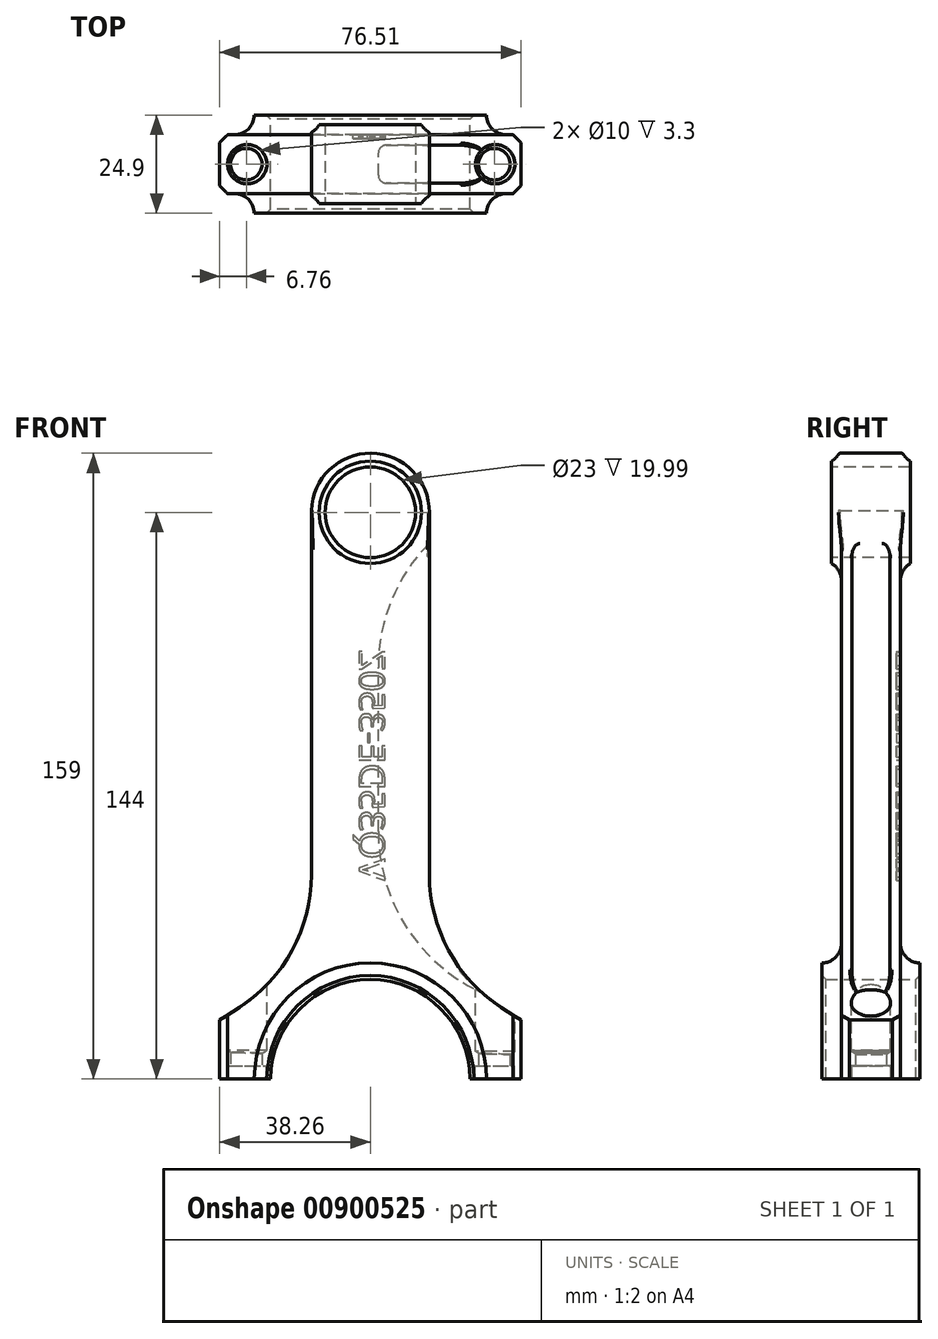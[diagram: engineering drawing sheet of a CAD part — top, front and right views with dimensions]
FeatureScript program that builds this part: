
annotation { "Feature Type Name" : "Feature", "Feature Type Description" : "" }
export const myFeature = defineFeature(function(context is Context, id is Id, definition is map)
    precondition{}
    {
        {
            var Q0;
            Q0=qCreatedBy(makeId("Front.planeOp"),FACE);
            var sketch = newSketch(context, id + "F0", { "sketchPlane" : qUnion([Q0])});
            skArc(sketch, "E0", {"start": v(15, 144) * mm, "mid": v(0.23, 159) * mm, "end": v(-15, 144.46) * mm});
            skLineSegment(sketch, "E1", {"start": v(25.3, 0) * mm, "end": v(38.25, 0) * mm});
            skArc(sketch, "E2", {"start": v(-15, 51.82) * mm, "mid": v(-19.85, 32.73) * mm, "end": v(-33.22, 18.27) * mm});
            skArc(sketch, "E3.MirrorCS", {"start": v(15, 51.82) * mm, "mid": v(19.85, 32.73) * mm, "end": v(33.22, 18.27) * mm});
            skLineSegment(sketch, "E4", {"start": v(-38.25, 0) * mm, "end": v(-25.3, 0) * mm});
            skArc(sketch, "E5", {"start": v(-25.3, 0) * mm, "mid": v(0, 25.3) * mm, "end": v(25.3, 0) * mm});
            skLineSegment(sketch, "E6", {"start": v(15, 144) * mm, "end": v(15, 51.82) * mm});
            skLineSegment(sketch, "E7", {"start": v(-15, 144.46) * mm, "end": v(-15, 51.82) * mm});
            skLineSegment(sketch, "E8", {"start": v(33.22, 18.27) * mm, "end": v(38.24, 15) * mm});
            skLineSegment(sketch, "E9", {"start": v(-33.22, 18.27) * mm, "end": v(-38.26, 15) * mm});
            skLineSegment(sketch, "E10", {"start": v(-38.25, 0) * mm, "end": v(-38.26, 15) * mm});
            skLineSegment(sketch, "E11", {"start": v(38.25, 0) * mm, "end": v(38.24, 15) * mm});
            skSolve(sketch);
        }
        {
            var Q0;
            Q0=makeQuery(id+"F0.imprint","IMPRINT",FACE,{"disambiguationData":[TD([[makeQuery(id+"F0.imprint","IMPRINT",EDGE,{"derivedFrom":sQuery(id+"F0.wireOp",EDGE,"E0")}),1.0]])]});
            extrude(context, id + "F1", {"entities" : qUnion([Q0]), "endBound" : BoundingType.SYMMETRIC, "depth" : 15 * mm, "offsetDistance" : 25 * mm});
        }
        {
            var Q0;
            Q0=qCreatedBy(makeId("Front.planeOp"),FACE);
            var sketch = newSketch(context, id + "F2", { "sketchPlane" : qUnion([Q0])});
            skCircle(sketch, "E12", {"center": v(0, 144) * mm, "radius": 13 * mm});
            skSolve(sketch);
        }
        {
            var Q0;
            Q0 = qSketchRegion(id + "F2", true);
            extrude(context, id + "F3", {"entities" : qUnion([Q0]), "operationType" : NewBodyOperationType.ADD, "endBound" : BoundingType.SYMMETRIC, "depth" : 19.99 * mm, "offsetDistance" : 25 * mm});
        }
        {
            var Q0;
            Q0=qCreatedBy(makeId("Front.planeOp"),FACE);
            var sketch = newSketch(context, id + "F4", { "sketchPlane" : qUnion([Q0])});
            skArc(sketch, "E13", {"start": v(29.5, 0) * mm, "mid": v(0, 29.5) * mm, "end": v(-29.5, 0) * mm});
            skArc(sketch, "E14", {"start": v(-25.3, 0) * mm, "mid": v(0, 25.3) * mm, "end": v(25.3, 0) * mm});
            skLineSegment(sketch, "E15", {"start": v(-29.5, 0) * mm, "end": v(-25.3, 0) * mm});
            skLineSegment(sketch, "E16", {"start": v(25.3, 0) * mm, "end": v(29.5, 0) * mm});
            skSolve(sketch);
        }
        {
            var Q0;
            Q0 = qSketchRegion(id + "F4", true);
            extrude(context, id + "F5", {"entities" : qUnion([Q0]), "operationType" : NewBodyOperationType.ADD, "endBound" : BoundingType.SYMMETRIC, "depth" : 24.9 * mm, "offsetDistance" : 25 * mm});
        }
        {
            var Q0;
            Q0=makeQuery(id+"F5.boolean.opBoolean","INTERSECT",EDGE,{"derivedFrom":[makeQuery(id+"F1.opExtrude","CAP_FACE",FACE,{"disambiguationData":[OSD([sQuery(id+"F0.wireOp",EDGE,"E0"),sQuery(id+"F0.wireOp",EDGE,"E1"),sQuery(id+"F0.wireOp",EDGE,"E2"),sQuery(id+"F0.wireOp",EDGE,"E3.MirrorCS"),sQuery(id+"F0.wireOp",EDGE,"E4"),sQuery(id+"F0.wireOp",EDGE,"E5"),sQuery(id+"F0.wireOp",EDGE,"E6"),sQuery(id+"F0.wireOp",EDGE,"E7"),sQuery(id+"F0.wireOp",EDGE,"E8"),sQuery(id+"F0.wireOp",EDGE,"E9"),sQuery(id+"F0.wireOp",EDGE,"E10"),sQuery(id+"F0.wireOp",EDGE,"E11")])],"isStart":false}),makeQuery(id+"F5.opExtrude","SWEPT_FACE",FACE,{"disambiguationData":[OSD([sQuery(id+"F4.wireOp",EDGE,"E13")])]})]});
            var Q1;
            Q1=makeQuery(id+"F3.boolean.opBoolean","INTERSECT",EDGE,{"derivedFrom":[makeQuery(id+"F1.opExtrude","CAP_FACE",FACE,{"disambiguationData":[OSD([sQuery(id+"F0.wireOp",EDGE,"E0"),sQuery(id+"F0.wireOp",EDGE,"E1"),sQuery(id+"F0.wireOp",EDGE,"E2"),sQuery(id+"F0.wireOp",EDGE,"E3.MirrorCS"),sQuery(id+"F0.wireOp",EDGE,"E4"),sQuery(id+"F0.wireOp",EDGE,"E5"),sQuery(id+"F0.wireOp",EDGE,"E6"),sQuery(id+"F0.wireOp",EDGE,"E7"),sQuery(id+"F0.wireOp",EDGE,"E8"),sQuery(id+"F0.wireOp",EDGE,"E9"),sQuery(id+"F0.wireOp",EDGE,"E10"),sQuery(id+"F0.wireOp",EDGE,"E11")])],"isStart":false}),makeQuery(id+"F3.opExtrude","SWEPT_FACE",FACE,{"disambiguationData":[OSD([sQuery(id+"F2.wireOp",EDGE,"E12")])]})]});
            var Q2;
            Q2=makeQuery(id+"F3.boolean.opBoolean","INTERSECT",EDGE,{"derivedFrom":[makeQuery(id+"F1.opExtrude","CAP_FACE",FACE,{"disambiguationData":[OSD([sQuery(id+"F0.wireOp",EDGE,"E0"),sQuery(id+"F0.wireOp",EDGE,"E1"),sQuery(id+"F0.wireOp",EDGE,"E2"),sQuery(id+"F0.wireOp",EDGE,"E3.MirrorCS"),sQuery(id+"F0.wireOp",EDGE,"E4"),sQuery(id+"F0.wireOp",EDGE,"E5"),sQuery(id+"F0.wireOp",EDGE,"E6"),sQuery(id+"F0.wireOp",EDGE,"E7"),sQuery(id+"F0.wireOp",EDGE,"E8"),sQuery(id+"F0.wireOp",EDGE,"E9"),sQuery(id+"F0.wireOp",EDGE,"E10"),sQuery(id+"F0.wireOp",EDGE,"E11")])],"isStart":true}),makeQuery(id+"F3.opExtrude","SWEPT_FACE",FACE,{"disambiguationData":[OSD([sQuery(id+"F2.wireOp",EDGE,"E12")])]})]});
            var Q3;
            Q3=makeQuery(id+"F5.boolean.opBoolean","INTERSECT",EDGE,{"derivedFrom":[makeQuery(id+"F1.opExtrude","CAP_FACE",FACE,{"disambiguationData":[OSD([sQuery(id+"F0.wireOp",EDGE,"E0"),sQuery(id+"F0.wireOp",EDGE,"E1"),sQuery(id+"F0.wireOp",EDGE,"E2"),sQuery(id+"F0.wireOp",EDGE,"E3.MirrorCS"),sQuery(id+"F0.wireOp",EDGE,"E4"),sQuery(id+"F0.wireOp",EDGE,"E5"),sQuery(id+"F0.wireOp",EDGE,"E6"),sQuery(id+"F0.wireOp",EDGE,"E7"),sQuery(id+"F0.wireOp",EDGE,"E8"),sQuery(id+"F0.wireOp",EDGE,"E9"),sQuery(id+"F0.wireOp",EDGE,"E10"),sQuery(id+"F0.wireOp",EDGE,"E11")])],"isStart":true}),makeQuery(id+"F5.opExtrude","SWEPT_FACE",FACE,{"disambiguationData":[OSD([sQuery(id+"F4.wireOp",EDGE,"E13")])]})]});
            fillet(context, id + "F6", {"entities" : qUnion([Q0, Q1, Q2, Q3]), "radius" : 5 * mm, "tangentPropagation" : true, "allowEdgeOverflow" : false});
        }
        {
            var Q0;
            Q0=makeQuery(id+"F5.boolean.opBoolean","MERGE",FACE,{"derivedFrom":[makeQuery(id+"F1.opExtrude","SWEPT_FACE",FACE,{"disambiguationData":[OSD([sQuery(id+"F0.wireOp",EDGE,"E4")])]}),makeQuery(id+"F5.opExtrude","SWEPT_FACE",FACE,{"disambiguationData":[OSD([sQuery(id+"F4.wireOp",EDGE,"E15")])]})]});
            var sketch = newSketch(context, id + "F7", { "sketchPlane" : qUnion([Q0])});
            skPoint(sketch, "E17", {"position": v(-31.5, 0) * mm});
            skPoint(sketch, "E18", {"position": v(31.5, 0) * mm});
            skSolve(sketch);
        }
        {
            var Q0;
            Q0=sQuery(id+"F7.wireOp",VERTEX,"E17");
            var Q1;
            Q1=sQuery(id+"F7.wireOp",VERTEX,"E18");
            var Q2;
            Q2=makeQuery(id+"F1.opExtrude","SWEPT_BODY",BODY,{"disambiguationData":[OSD([sQuery(id+"F0.wireOp",EDGE,"E0"),sQuery(id+"F0.wireOp",EDGE,"E1"),sQuery(id+"F0.wireOp",EDGE,"E2"),sQuery(id+"F0.wireOp",EDGE,"E3.MirrorCS"),sQuery(id+"F0.wireOp",EDGE,"E4"),sQuery(id+"F0.wireOp",EDGE,"E5"),sQuery(id+"F0.wireOp",EDGE,"E6"),sQuery(id+"F0.wireOp",EDGE,"E7"),sQuery(id+"F0.wireOp",EDGE,"E8"),sQuery(id+"F0.wireOp",EDGE,"E9"),sQuery(id+"F0.wireOp",EDGE,"E10"),sQuery(id+"F0.wireOp",EDGE,"E11")])]});
            hole(context, id + "F8", {"style" : HoleStyle.C_BORE, "endStyle" : HoleEndStyle.THROUGH, "holeDiameter" : 8 * mm, "cBoreDiameter" : 10 * mm, "cBoreDepth" : 3.3 * mm, "majorDiameter" : 5 * mm, "isTappedThrough" : true, "tappedDepth" : 12 * mm, "tapClearance" : 3, "locations" : qUnion([Q0, Q1]), "scope" : qUnion([Q2])});
        }
        {
            var Q0;
            Q0=makeQuery(id+"F5.boolean.opBoolean","MERGE",FACE,{"derivedFrom":[makeQuery(id+"F1.opExtrude","SWEPT_FACE",FACE,{"disambiguationData":[OSD([sQuery(id+"F0.wireOp",EDGE,"E4")])]}),makeQuery(id+"F5.opExtrude","SWEPT_FACE",FACE,{"disambiguationData":[OSD([sQuery(id+"F4.wireOp",EDGE,"E15")])]})]});
            cPlane(context, id + "F9", {"entities" : qUnion([Q0]), "cplaneType" : CPlaneType.OFFSET, "offset" : 25 * mm, "oppositeDirection" : true, "width" : 150 * mm, "height" : 150 * mm});
        }
        {
            var Q0;
            Q0=qCreatedBy(id+"F9.planeOp",FACE);
            var sketch = newSketch(context, id + "F10", { "sketchPlane" : qUnion([Q0])});
            skPoint(sketch, "E19", {"position": v(-31.27, 0) * mm});
            skPoint(sketch, "E20", {"position": v(31.73, 0) * mm});
            skSolve(sketch);
        }
        {
            var Q0;
            Q0=sQuery(id+"F10.wireOp",VERTEX,"E19");
            var Q1;
            Q1=sQuery(id+"F10.wireOp",VERTEX,"E20");
            var Q2;
            Q2=makeQuery(id+"F1.opExtrude","SWEPT_BODY",BODY,{"disambiguationData":[OSD([sQuery(id+"F0.wireOp",EDGE,"E0"),sQuery(id+"F0.wireOp",EDGE,"E1"),sQuery(id+"F0.wireOp",EDGE,"E2"),sQuery(id+"F0.wireOp",EDGE,"E3.MirrorCS"),sQuery(id+"F0.wireOp",EDGE,"E4"),sQuery(id+"F0.wireOp",EDGE,"E5"),sQuery(id+"F0.wireOp",EDGE,"E6"),sQuery(id+"F0.wireOp",EDGE,"E7"),sQuery(id+"F0.wireOp",EDGE,"E8"),sQuery(id+"F0.wireOp",EDGE,"E9"),sQuery(id+"F0.wireOp",EDGE,"E10"),sQuery(id+"F0.wireOp",EDGE,"E11")])]});
            hole(context, id + "F11", {"style" : HoleStyle.SIMPLE, "endStyle" : HoleEndStyle.BLIND, "oppositeDirection" : true, "holeDiameter" : 10 * mm, "majorDiameter" : 5 * mm, "holeDepth" : 9 * mm, "isTappedThrough" : true, "tappedDepth" : 12 * mm, "tapClearance" : 3, "locations" : qUnion([Q0, Q1]), "scope" : qUnion([Q2])});
        }
        {
            var Q0;
            Q0=makeQuery(id+"F3.opExtrude","CAP_FACE",FACE,{"disambiguationData":[OSD([sQuery(id+"F2.wireOp",EDGE,"E12")])],"isStart":false});
            var sketch = newSketch(context, id + "F12", { "sketchPlane" : qUnion([Q0])});
            skPoint(sketch, "E21", {"position": v(0, 144) * mm});
            skSolve(sketch);
        }
        {
            var Q0;
            Q0=sQuery(id+"F12.wireOp",VERTEX,"E21");
            var Q1;
            Q1=makeQuery(id+"F1.opExtrude","SWEPT_BODY",BODY,{"disambiguationData":[OSD([sQuery(id+"F0.wireOp",EDGE,"E0"),sQuery(id+"F0.wireOp",EDGE,"E1"),sQuery(id+"F0.wireOp",EDGE,"E2"),sQuery(id+"F0.wireOp",EDGE,"E3.MirrorCS"),sQuery(id+"F0.wireOp",EDGE,"E4"),sQuery(id+"F0.wireOp",EDGE,"E5"),sQuery(id+"F0.wireOp",EDGE,"E6"),sQuery(id+"F0.wireOp",EDGE,"E7"),sQuery(id+"F0.wireOp",EDGE,"E8"),sQuery(id+"F0.wireOp",EDGE,"E9"),sQuery(id+"F0.wireOp",EDGE,"E10"),sQuery(id+"F0.wireOp",EDGE,"E11")])]});
            hole(context, id + "F13", {"style" : HoleStyle.SIMPLE, "endStyle" : HoleEndStyle.THROUGH, "holeDiameter" : 23 * mm, "majorDiameter" : 5 * mm, "isTappedThrough" : true, "tappedDepth" : 12 * mm, "tapClearance" : 3, "locations" : qUnion([Q0]), "scope" : qUnion([Q1])});
        }
        {
            var Q0;
            Q0=qCreatedBy(makeId("Front.planeOp"),FACE);
            var sketch = newSketch(context, id + "F14", { "sketchPlane" : qUnion([Q0])});
            skArc(sketch, "E22", {"start": v(2.03, 62.88) * mm, "mid": v(9.36, 38.26) * mm, "end": v(28.96, 21.67) * mm});
            skCircle(sketch, "E23", {"center": v(0, 0) * mm, "radius": 25.3 * mm, "construction": true});
            skLineSegment(sketch, "E24", {"start": v(29.55, 7.8) * mm, "end": v(-8.31, 40.83) * mm, "construction": true});
            skLineSegment(sketch, "E25", {"start": v(35.49, 13.23) * mm, "end": v(-8.31, 51.45) * mm, "construction": true});
            skArc(sketch, "E26", {"start": v(15, 136.23) * mm, "mid": v(5.4, 121.7) * mm, "end": v(2.03, 104.62) * mm});
            skLineSegment(sketch, "E27", {"start": v(2.03, 62.88) * mm, "end": v(2.03, 104.62) * mm});
            skArc(sketch, "E28", {"start": v(15, 52.03) * mm, "mid": v(18.66, 35.32) * mm, "end": v(28.96, 21.67) * mm});
            skLineSegment(sketch, "E29.0", {"start": v(15, 136.23) * mm, "end": v(15, 51.82) * mm});
            skPoint(sketch, "E30.orphan", {"position": v(15, 144) * mm});
            skLineSegment(sketch, "E31", {"start": v(0, 0) * mm, "end": v(0, 56.7) * mm, "construction": true});
            skArc(sketch, "E32.MirrorCS", {"start": v(-2.03, 62.88) * mm, "mid": v(-9.36, 38.26) * mm, "end": v(-28.96, 21.67) * mm});
            skLineSegment(sketch, "E33.MirrorCS", {"start": v(-2.03, 62.88) * mm, "end": v(-2.03, 104.62) * mm});
            skArc(sketch, "E34.MirrorCS", {"start": v(-15, 136.23) * mm, "mid": v(-5.4, 121.7) * mm, "end": v(-2.03, 104.62) * mm});
            skLineSegment(sketch, "E35.MirrorCS", {"start": v(-15, 136.23) * mm, "end": v(-15, 51.82) * mm});
            skArc(sketch, "E36.MirrorCS", {"start": v(-15, 52.03) * mm, "mid": v(-18.66, 35.32) * mm, "end": v(-28.96, 21.67) * mm});
            skSolve(sketch);
        }
        {
            var Q0;
            Q0=makeQuery(id+"F14.imprint","IMPRINT",FACE,{"disambiguationData":[TD([[makeQuery(id+"F14.imprint","IMPRINT",EDGE,{"derivedFrom":sQuery(id+"F14.wireOp",EDGE,"E22")}),1.0]])]});
            var Q1;
            Q1=makeQuery(id+"F14.imprint","IMPRINT",FACE,{"disambiguationData":[TD([[makeQuery(id+"F14.imprint","IMPRINT",EDGE,{"derivedFrom":sQuery(id+"F14.wireOp",EDGE,"E32.MirrorCS")}),-1.0]])]});
            extrude(context, id + "F15", {"entities" : qUnion([Q0, Q1]), "operationType" : NewBodyOperationType.REMOVE, "endBound" : BoundingType.SYMMETRIC, "depth" : 9.65 * mm, "offsetDistance" : 25 * mm});
        }
        {
            var Q0;
            Q0=makeQuery(id+"F15.boolean.opBoolean","COPY",EDGE,{"derivedFrom":makeQuery(id+"F15.opExtrude","CAP_EDGE",EDGE,{"disambiguationData":[OSD([sQuery(id+"F14.wireOp",EDGE,"E33.MirrorCS")])],"isStart":false})});
            var Q1;
            Q1=makeQuery(id+"F15.boolean.opBoolean","COPY",EDGE,{"derivedFrom":makeQuery(id+"F15.opExtrude","CAP_EDGE",EDGE,{"disambiguationData":[OSD([sQuery(id+"F14.wireOp",EDGE,"E33.MirrorCS")])],"isStart":true})});
            var Q2;
            Q2=makeQuery(id+"F15.boolean.opBoolean","COPY",EDGE,{"derivedFrom":makeQuery(id+"F15.opExtrude","CAP_EDGE",EDGE,{"disambiguationData":[OSD([sQuery(id+"F14.wireOp",EDGE,"E27")])],"isStart":false})});
            var Q3;
            Q3=makeQuery(id+"F15.boolean.opBoolean","COPY",EDGE,{"derivedFrom":makeQuery(id+"F15.opExtrude","CAP_EDGE",EDGE,{"disambiguationData":[OSD([sQuery(id+"F14.wireOp",EDGE,"E27")])],"isStart":true})});
            fillet(context, id + "F16", {"entities" : qUnion([Q0, Q1, Q2, Q3]), "radius" : 2 * mm, "tangentPropagation" : true, "allowEdgeOverflow" : false});
        }
        {
            var Q0;
            Q0=makeQuery(id+"F15.boolean.opBoolean","INTERSECT",EDGE,{"derivedFrom":[makeQuery(id+"F1.opExtrude","SWEPT_FACE",FACE,{"disambiguationData":[OSD([sQuery(id+"F0.wireOp",EDGE,"E3.MirrorCS")])]}),makeQuery(id+"F15.opExtrude","CAP_FACE",FACE,{"disambiguationData":[OSD([sQuery(id+"F14.wireOp",EDGE,"E22"),sQuery(id+"F14.wireOp",EDGE,"E26"),sQuery(id+"F14.wireOp",EDGE,"E27"),sQuery(id+"F14.wireOp",EDGE,"E28"),sQuery(id+"F14.wireOp",EDGE,"E29.0")])],"isStart":true})]});
            var Q1;
            Q1=makeQuery(id+"F15.boolean.opBoolean","INTERSECT",EDGE,{"derivedFrom":[makeQuery(id+"F1.opExtrude","SWEPT_FACE",FACE,{"disambiguationData":[OSD([sQuery(id+"F0.wireOp",EDGE,"E2")])]}),makeQuery(id+"F15.opExtrude","CAP_FACE",FACE,{"disambiguationData":[OSD([sQuery(id+"F14.wireOp",EDGE,"E32.MirrorCS"),sQuery(id+"F14.wireOp",EDGE,"E33.MirrorCS"),sQuery(id+"F14.wireOp",EDGE,"E34.MirrorCS"),sQuery(id+"F14.wireOp",EDGE,"E35.MirrorCS"),sQuery(id+"F14.wireOp",EDGE,"E36.MirrorCS")])],"isStart":false})]});
            fillet(context, id + "F17", {"entities" : qUnion([Q0, Q1]), "radius" : 0.5 * mm, "tangentPropagation" : true, "allowEdgeOverflow" : false});
        }
        {
            var Q0;
            Q0=makeQuery(id+"F1.opExtrude","CAP_EDGE",EDGE,{"disambiguationData":[OSD([sQuery(id+"F0.wireOp",EDGE,"E7")])],"isStart":true});
            var Q1;
            Q1=makeQuery(id+"F1.opExtrude","CAP_EDGE",EDGE,{"disambiguationData":[OSD([sQuery(id+"F0.wireOp",EDGE,"E6")])],"isStart":true});
            var Q2;
            Q2=makeQuery(id+"F1.opExtrude","CAP_EDGE",EDGE,{"disambiguationData":[OSD([sQuery(id+"F0.wireOp",EDGE,"E7")])],"isStart":false});
            var Q3;
            Q3=makeQuery(id+"F1.opExtrude","CAP_EDGE",EDGE,{"disambiguationData":[OSD([sQuery(id+"F0.wireOp",EDGE,"E6")])],"isStart":false});
            fillet(context, id + "F18", {"entities" : qUnion([Q0, Q1, Q2, Q3]), "radius" : 0.5 * mm, "tangentPropagation" : true, "allowEdgeOverflow" : false});
        }
        {
            var Q0;
            Q0=makeQuery(id+"F1.opExtrude","CAP_EDGE",EDGE,{"disambiguationData":[OSD([sQuery(id+"F0.wireOp",EDGE,"E10")])],"isStart":false});
            var Q1;
            Q1=makeQuery(id+"F1.opExtrude","CAP_EDGE",EDGE,{"disambiguationData":[OSD([sQuery(id+"F0.wireOp",EDGE,"E11")])],"isStart":false});
            var Q2;
            Q2=makeQuery(id+"F1.opExtrude","CAP_EDGE",EDGE,{"disambiguationData":[OSD([sQuery(id+"F0.wireOp",EDGE,"E10")])],"isStart":true});
            var Q3;
            Q3=makeQuery(id+"F1.opExtrude","CAP_EDGE",EDGE,{"disambiguationData":[OSD([sQuery(id+"F0.wireOp",EDGE,"E11")])],"isStart":true});
            chamfer(context, id + "F19", {"entities" : qUnion([Q0, Q1, Q2, Q3]), "width" : 2 * mm});
        }
        {
            var Q0;
            Q0=makeQuery(id+"F1.opExtrude","CAP_FACE",FACE,{"disambiguationData":[OSD([sQuery(id+"F0.wireOp",EDGE,"E0"),sQuery(id+"F0.wireOp",EDGE,"E1"),sQuery(id+"F0.wireOp",EDGE,"E2"),sQuery(id+"F0.wireOp",EDGE,"E3.MirrorCS"),sQuery(id+"F0.wireOp",EDGE,"E4"),sQuery(id+"F0.wireOp",EDGE,"E5"),sQuery(id+"F0.wireOp",EDGE,"E6"),sQuery(id+"F0.wireOp",EDGE,"E7"),sQuery(id+"F0.wireOp",EDGE,"E8"),sQuery(id+"F0.wireOp",EDGE,"E9"),sQuery(id+"F0.wireOp",EDGE,"E10"),sQuery(id+"F0.wireOp",EDGE,"E11")])],"isStart":true});
            var sketch = newSketch(context, id + "F20", { "sketchPlane" : qUnion([Q0])});
            skText(sketch, "E37", { "text": "VQ35DE-350Z", "fontName": "OpenSans-Regular.ttf"});
            const initialGuessF20  = {"E37": [0.00284, 0.0505, 0, 1, 0.00657]};
            skSetInitialGuess(sketch, initialGuessF20);
            skSolve(sketch);
        }
        {
            var Q0;
            Q0 = qSketchRegion(id + "F20", true);
            extrude(context, id + "F21", {"entities" : qUnion([Q0]), "operationType" : NewBodyOperationType.REMOVE, "oppositeDirection" : true, "depth" : 1 * mm, "offsetDistance" : 25 * mm});
        }
        {
            var Q0;
            Q0=makeQuery(id+"F5.opExtrude","CAP_EDGE",EDGE,{"disambiguationData":[OSD([sQuery(id+"F4.wireOp",EDGE,"E14")])],"isStart":false});
            var Q1;
            Q1=makeQuery(id+"F5.opExtrude","CAP_EDGE",EDGE,{"disambiguationData":[OSD([sQuery(id+"F4.wireOp",EDGE,"E14")])],"isStart":true});
            chamfer(context, id + "F22", {"entities" : qUnion([Q0, Q1]), "width" : 1 * mm, "tangentPropagation" : true});
        }
    });
